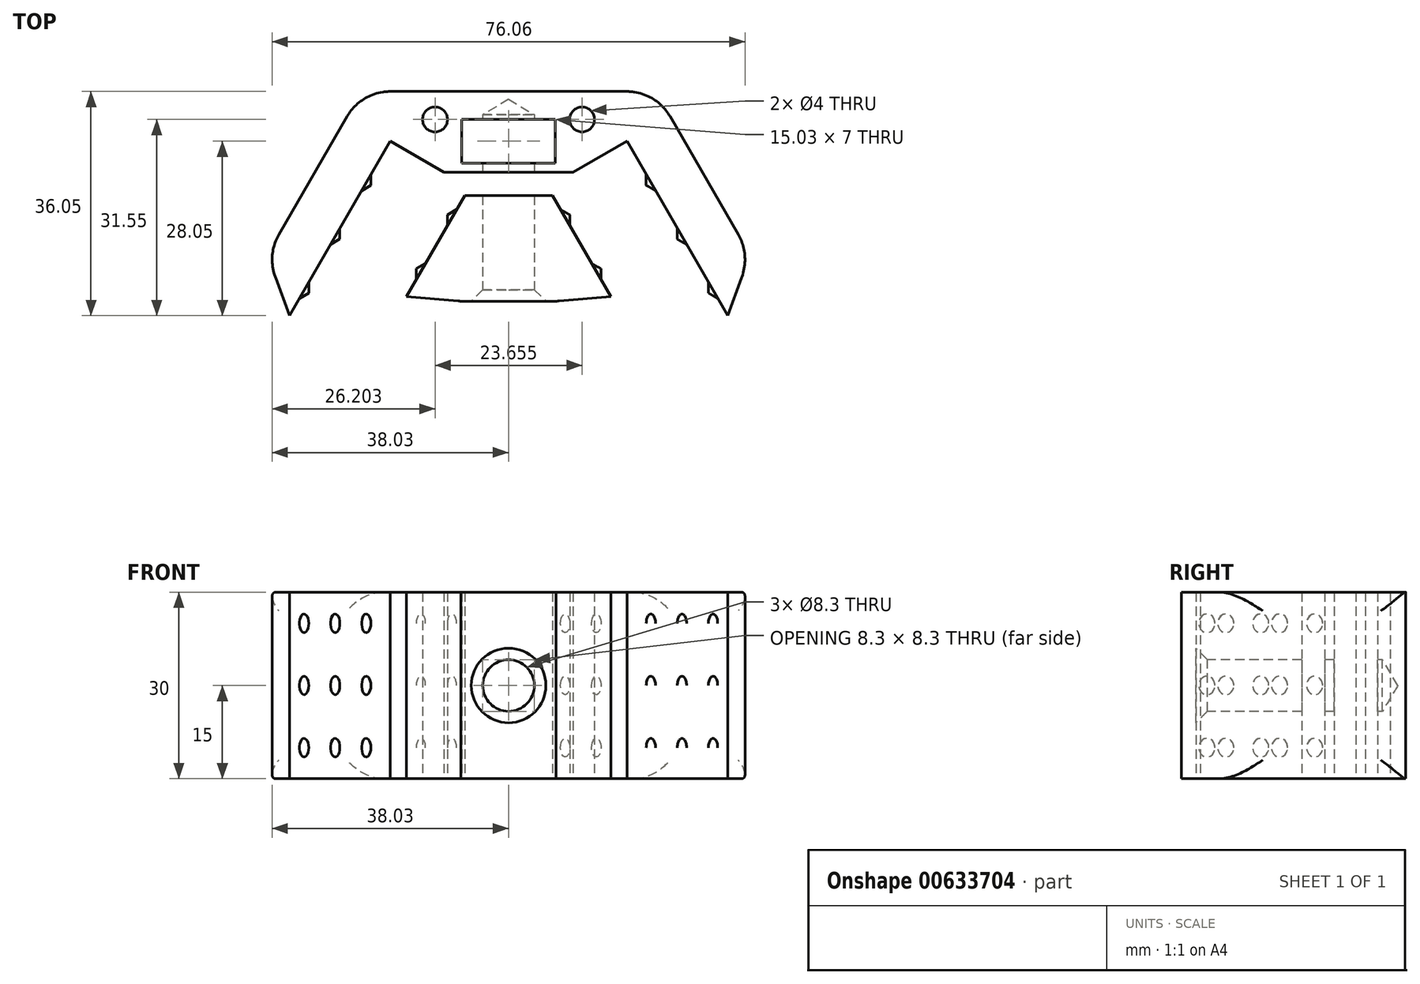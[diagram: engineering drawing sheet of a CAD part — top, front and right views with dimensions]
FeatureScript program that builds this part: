
annotation { "Feature Type Name" : "Feature", "Feature Type Description" : "" }
export const myFeature = defineFeature(function(context is Context, id is Id, definition is map)
    precondition{}
    {
        {
            var Q0;
            Q0=qCreatedBy(makeId("Top.planeOp"),FACE);
            var sketch = newSketch(context, id + "F0", { "sketchPlane" : qUnion([Q0])});
            skLineSegment(sketch, "E0", {"start": v(-3.45, 0) * mm, "end": v(3.45, 0) * mm, "construction": true});
            skLineSegment(sketch, "E1.bottom", {"start": v(3.45, 0) * mm, "end": v(7.06, -6.25) * mm, "construction": true});
            skLineSegment(sketch, "E1.top", {"start": v(19.04, 9) * mm, "end": v(70.61, -80.32) * mm});
            skLineSegment(sketch, "E1.left", {"start": v(3.45, 0) * mm, "end": v(10.38, 4) * mm, "construction": true});
            skLineSegment(sketch, "E2.bottom", {"start": v(-3.45, 0) * mm, "end": v(-7.06, -6.25) * mm, "construction": true});
            skLineSegment(sketch, "E2.top", {"start": v(-19.04, 9) * mm, "end": v(-70.62, -80.34) * mm});
            skLineSegment(sketch, "E2.left", {"start": v(-3.45, 0) * mm, "end": v(-10.38, 4) * mm, "construction": true});
            skLineSegment(sketch, "E3", {"start": v(0, 0) * mm, "end": v(0, 18.24) * mm, "construction": true});
            skLineSegment(sketch, "E4", {"start": v(-19.04, 9) * mm, "end": v(19.04, 9) * mm, "construction": true});
            skLineSegment(sketch, "E5.0", {"start": v(23.66, 17) * mm, "end": v(77.54, -76.32) * mm});
            skLineSegment(sketch, "E5.1", {"start": v(-23.66, 17) * mm, "end": v(23.66, 17) * mm});
            skLineSegment(sketch, "E5.2", {"start": v(-23.66, 17) * mm, "end": v(-77.55, -76.34) * mm});
            skPoint(sketch, "E6", {"position": v(-38.83, -9.27) * mm});
            skLineSegment(sketch, "E7", {"start": v(-38.83, -9.27) * mm, "end": v(-35.24, -19.05) * mm});
            skLineSegment(sketch, "E8.MirrorCS", {"start": v(38.83, -9.27) * mm, "end": v(35.24, -19.05) * mm});
            skLineSegment(sketch, "E9.0", {"start": v(1.16, -8) * mm, "end": v(-48.1, -93.34) * mm});
            skLineSegment(sketch, "E9.1", {"start": v(-1.16, -8) * mm, "end": v(1.16, -8) * mm});
            skLineSegment(sketch, "E9.2", {"start": v(-1.16, -8) * mm, "end": v(48.1, -93.32) * mm});
            skLineSegment(sketch, "E10", {"start": v(-16.45, -22.52) * mm, "end": v(-7.63, -23.24) * mm});
            skLineSegment(sketch, "E11.MirrorCS", {"start": v(16.45, -22.52) * mm, "end": v(7.63, -23.24) * mm});
            skLineSegment(sketch, "E12", {"start": v(-7.64, -23.25) * mm, "end": v(7.64, -23.25) * mm});
            skLineSegment(sketch, "E13", {"start": v(-10.38, 4) * mm, "end": v(10.38, 4) * mm});
            skLineSegment(sketch, "E14", {"start": v(-7.06, -6.25) * mm, "end": v(7.06, -6.25) * mm});
            skLineSegment(sketch, "E15.bottom", {"start": v(7.51, 12.5) * mm, "end": v(-7.51, 12.5) * mm});
            skLineSegment(sketch, "E15.top", {"start": v(7.51, 5.5) * mm, "end": v(-7.51, 5.5) * mm});
            skLineSegment(sketch, "E15.left", {"start": v(7.51, 12.5) * mm, "end": v(7.51, 5.5) * mm});
            skLineSegment(sketch, "E15.right", {"start": v(-7.51, 12.5) * mm, "end": v(-7.51, 5.5) * mm});
            skPoint(sketch, "E15.middle", {"position": v(0, 9) * mm});
            skCircle(sketch, "E16", {"center": v(-11.83, 12.5) * mm, "radius": 2 * mm});
            skCircle(sketch, "E17.MirrorC", {"center": v(11.83, 12.5) * mm, "radius": 2 * mm});
            skLineSegment(sketch, "E18", {"start": v(-10.38, 4) * mm, "end": v(-19.04, 9) * mm});
            skLineSegment(sketch, "E19", {"start": v(-7.06, -6.25) * mm, "end": v(-55.03, -89.34) * mm});
            skLineSegment(sketch, "E20", {"start": v(7.06, -6.25) * mm, "end": v(55.02, -89.32) * mm});
            skLineSegment(sketch, "E21", {"start": v(10.38, 4) * mm, "end": v(19.04, 9) * mm});
            skSolve(sketch);
        }
        {
            var Q0;
            {var subQ9=sQuery(id+"F0.wireOp",EDGE,"E5.1");Q0=makeQuery(id+"F0.imprint","IMPRINT",FACE,{"disambiguationData":[TD([[makeQuery(id+"F0.imprint","IMPRINT",EDGE,{"derivedFrom":subQ9}),-1.0]])]});}
            var Q1;
            {var subQ0=sQuery(id+"F0.wireOp",EDGE,"E10");Q1=makeQuery(id+"F0.imprint","IMPRINT",FACE,{"disambiguationData":[TD([[makeQuery(id+"F0.imprint","IMPRINT",EDGE,{"derivedFrom":subQ0}),1.0]])]});}
            var Q2;
            {var subQ0=sQuery(id+"F0.wireOp",EDGE,"E9.1");Q2=makeQuery(id+"F0.imprint","IMPRINT",FACE,{"disambiguationData":[TD([[makeQuery(id+"F0.imprint","IMPRINT",EDGE,{"derivedFrom":subQ0}),-1.0]])]});}
            var Q3;
            {var subQ5=sQuery(id+"F0.wireOp",EDGE,"E12");Q3=makeQuery(id+"F0.imprint","IMPRINT",FACE,{"disambiguationData":[TD([[makeQuery(id+"F0.imprint","IMPRINT",EDGE,{"derivedFrom":subQ5}),1.0]])]});}
            extrude(context, id + "F1", {"entities" : qUnion([Q0, Q1, Q2, Q3]), "depth" : 30 * mm, "offsetDistance" : 25 * mm});
        }
        {
            var Q0;
            Q0=makeQuery(id+"F1.opExtrude","SWEPT_FACE",FACE,{"disambiguationData":[OSD([sQuery(id+"F0.wireOp",EDGE,"E12")])]});
            var sketch = newSketch(context, id + "F2", { "sketchPlane" : qUnion([Q0])});
            skPoint(sketch, "E22", {"position": v(0, 15) * mm});
            skPoint(sketch, "E22.positionSnap0", {"position": v(0, 30) * mm});
            skPoint(sketch, "E22.positionSnap1", {"position": v(-7.64, 15) * mm});
            skSolve(sketch);
        }
        {
            var Q0;
            Q0=sQuery(id+"F2.wireOp",VERTEX,"E22");
            var Q1;
            Q1=makeQuery(id+"F1.opExtrude","SWEPT_BODY",BODY,{"disambiguationData":[OSD([sQuery(id+"F0.wireOp",EDGE,"E1.top"),sQuery(id+"F0.wireOp",EDGE,"E2.top"),sQuery(id+"F0.wireOp",EDGE,"E5.0"),sQuery(id+"F0.wireOp",EDGE,"E5.1"),sQuery(id+"F0.wireOp",EDGE,"E5.2"),sQuery(id+"F0.wireOp",EDGE,"E7"),sQuery(id+"F0.wireOp",EDGE,"E8.MirrorCS"),sQuery(id+"F0.wireOp",EDGE,"E13"),sQuery(id+"F0.wireOp",EDGE,"E15.bottom"),sQuery(id+"F0.wireOp",EDGE,"E15.top"),sQuery(id+"F0.wireOp",EDGE,"E15.left"),sQuery(id+"F0.wireOp",EDGE,"E15.right"),sQuery(id+"F0.wireOp",EDGE,"E16"),sQuery(id+"F0.wireOp",EDGE,"E17.MirrorC"),sQuery(id+"F0.wireOp",EDGE,"E18"),sQuery(id+"F0.wireOp",EDGE,"E21")])]});
            var Q2;
            Q2=makeQuery(id+"F1.opExtrude","SWEPT_BODY",BODY,{"disambiguationData":[OSD([sQuery(id+"F0.wireOp",EDGE,"E9.0"),sQuery(id+"F0.wireOp",EDGE,"E9.2"),sQuery(id+"F0.wireOp",EDGE,"E10"),sQuery(id+"F0.wireOp",EDGE,"E11.MirrorCS"),sQuery(id+"F0.wireOp",EDGE,"E12"),sQuery(id+"F0.wireOp",EDGE,"E14"),sQuery(id+"F0.wireOp",EDGE,"E19"),sQuery(id+"F0.wireOp",EDGE,"E20")])]});
            hole(context, id + "F3", {"style" : HoleStyle.C_SINK, "endStyle" : HoleEndStyle.BLIND, "holeDiameter" : 8.3 * mm, "cSinkDiameter" : 12 * mm, "cSinkAngle" : 90 * degree, "majorDiameter" : 5 * mm, "holeDepth" : 36.5 * mm, "isTappedThrough" : true, "tappedDepth" : 12 * mm, "tapClearance" : 3, "startFromSketch" : true, "locations" : qUnion([Q0]), "scope" : qUnion([Q1, Q2])});
        }
        {
            var Q0;
            Q0=makeQuery(id+"F1.opExtrude","SWEPT_EDGE",EDGE,{"disambiguationData":[OSD([sQuery(id+"F0.wireOp",EDGE,"E5.2"),sQuery(id+"F0.wireOp",EDGE,"E7")])]});
            var Q1;
            Q1=makeQuery(id+"F1.opExtrude","SWEPT_EDGE",EDGE,{"disambiguationData":[OSD([sQuery(id+"F0.wireOp",EDGE,"E5.1"),sQuery(id+"F0.wireOp",EDGE,"E5.2")])]});
            var Q2;
            Q2=makeQuery(id+"F1.opExtrude","SWEPT_EDGE",EDGE,{"disambiguationData":[OSD([sQuery(id+"F0.wireOp",EDGE,"E5.0"),sQuery(id+"F0.wireOp",EDGE,"E5.1")])]});
            var Q3;
            Q3=makeQuery(id+"F1.opExtrude","SWEPT_EDGE",EDGE,{"disambiguationData":[OSD([sQuery(id+"F0.wireOp",EDGE,"E5.0"),sQuery(id+"F0.wireOp",EDGE,"E8.MirrorCS")])]});
            fillet(context, id + "F4", {"entities" : qUnion([Q0, Q1, Q2, Q3]), "radius" : 8 * mm, "tangentPropagation" : true, "allowEdgeOverflow" : false});
        }
        {
            var Q0;
            Q0=makeQuery(id+"F1.opExtrude","CAP_EDGE",EDGE,{"disambiguationData":[OSD([sQuery(id+"F0.wireOp",EDGE,"E5.0")])],"isStart":false});
            var Q1;
            Q1=makeQuery(id+"F1.opExtrude","CAP_EDGE",EDGE,{"disambiguationData":[OSD([sQuery(id+"F0.wireOp",EDGE,"E5.2")])],"isStart":false});
            var Q2;
            Q2=makeQuery(id+"F1.opExtrude","CAP_EDGE",EDGE,{"disambiguationData":[OSD([sQuery(id+"F0.wireOp",EDGE,"E5.0")])],"isStart":true});
            var Q3;
            Q3=makeQuery(id+"F1.opExtrude","CAP_EDGE",EDGE,{"disambiguationData":[OSD([sQuery(id+"F0.wireOp",EDGE,"E5.2")])],"isStart":true});
            fillet(context, id + "F5", {"entities" : qUnion([Q0, Q1, Q2, Q3]), "radius" : 3 * mm, "allowEdgeOverflow" : false});
        }
        {
            var Q0;
            Q0=makeQuery(id+"F1.opExtrude","SWEPT_EDGE",EDGE,{"disambiguationData":[OSD([sQuery(id+"F0.wireOp",EDGE,"E9.0"),sQuery(id+"F0.wireOp",EDGE,"E10")])]});
            var Q1;
            Q1=makeQuery(id+"F1.opExtrude","SWEPT_EDGE",EDGE,{"disambiguationData":[OSD([sQuery(id+"F0.wireOp",EDGE,"E9.2"),sQuery(id+"F0.wireOp",EDGE,"E11.MirrorCS")])]});
            fillet(context, id + "F6", {"entities" : qUnion([Q0, Q1]), "radius" : 10 * mm, "tangentPropagation" : true, "allowEdgeOverflow" : false});
        }
        {
            var Q0;
            Q0=makeQuery(id+"F1.opExtrude","SWEPT_FACE",FACE,{"disambiguationData":[OSD([sQuery(id+"F0.wireOp",EDGE,"E2.top")])]});
            var sketch = newSketch(context, id + "F7", { "sketchPlane" : qUnion([Q0])});
            skCircle(sketch, "E23", {"center": v(-29.42, 25) * mm, "radius": 1.5 * mm});
            skCircle(sketch, "E24.0.1.0", {"center": v(-29.42, 15) * mm, "radius": 1.5 * mm});
            skCircle(sketch, "E24.0.2.0", {"center": v(-29.42, 5) * mm, "radius": 1.5 * mm});
            skCircle(sketch, "E24.1.0.0", {"center": v(-19.42, 25) * mm, "radius": 1.5 * mm});
            skCircle(sketch, "E24.1.1.0", {"center": v(-19.42, 15) * mm, "radius": 1.5 * mm});
            skCircle(sketch, "E24.1.2.0", {"center": v(-19.42, 5) * mm, "radius": 1.5 * mm});
            skCircle(sketch, "E24.2.0.0", {"center": v(-9.42, 25) * mm, "radius": 1.5 * mm});
            skCircle(sketch, "E24.2.1.0", {"center": v(-9.42, 15) * mm, "radius": 1.5 * mm});
            skCircle(sketch, "E24.2.2.0", {"center": v(-9.42, 5) * mm, "radius": 1.5 * mm});
            skLineSegment(sketch, "E24.direction1", {"start": v(-29.42, 25) * mm, "end": v(-19.42, 25) * mm, "construction": true});
            skLineSegment(sketch, "E24.direction2", {"start": v(-29.42, 25) * mm, "end": v(-29.42, 15) * mm, "construction": true});
            skLineSegment(sketch, "E25", {"start": v(-29.42, 25) * mm, "end": v(-34.12, 25) * mm, "construction": true});
            skLineSegment(sketch, "E26", {"start": v(-29.42, 25) * mm, "end": v(-29.42, 30) * mm, "construction": true});
            skSolve(sketch);
        }
        {
            var Q0;
            Q0=makeQuery(id+"F1.opExtrude","SWEPT_FACE",FACE,{"disambiguationData":[OSD([sQuery(id+"F0.wireOp",EDGE,"E1.top")])]});
            var sketch = newSketch(context, id + "F8", { "sketchPlane" : qUnion([Q0])});
            skCircle(sketch, "E27", {"center": v(9.42, 25) * mm, "radius": 1.5 * mm});
            skCircle(sketch, "E28.0.1.0", {"center": v(9.42, 15) * mm, "radius": 1.5 * mm});
            skCircle(sketch, "E28.0.2.0", {"center": v(9.42, 5) * mm, "radius": 1.5 * mm});
            skCircle(sketch, "E28.1.0.0", {"center": v(19.42, 25) * mm, "radius": 1.5 * mm});
            skCircle(sketch, "E28.1.1.0", {"center": v(19.42, 15) * mm, "radius": 1.5 * mm});
            skCircle(sketch, "E28.1.2.0", {"center": v(19.42, 5) * mm, "radius": 1.5 * mm});
            skCircle(sketch, "E28.2.0.0", {"center": v(29.42, 25) * mm, "radius": 1.5 * mm});
            skCircle(sketch, "E28.2.1.0", {"center": v(29.42, 15) * mm, "radius": 1.5 * mm});
            skCircle(sketch, "E28.2.2.0", {"center": v(29.42, 5) * mm, "radius": 1.5 * mm});
            skLineSegment(sketch, "E28.direction1", {"start": v(9.42, 25) * mm, "end": v(19.42, 25) * mm, "construction": true});
            skLineSegment(sketch, "E28.direction2", {"start": v(9.42, 25) * mm, "end": v(9.42, 15) * mm, "construction": true});
            skLineSegment(sketch, "E29", {"start": v(29.42, 25) * mm, "end": v(34.12, 25) * mm, "construction": true});
            skLineSegment(sketch, "E30", {"start": v(34.12, 25) * mm, "end": v(29.42, 25) * mm, "construction": true});
            skLineSegment(sketch, "E31", {"start": v(29.42, 25) * mm, "end": v(29.42, 30) * mm, "construction": true});
            skSolve(sketch);
        }
        {
            var Q0;
            Q0=makeQuery(id+"F1.opExtrude","SWEPT_FACE",FACE,{"disambiguationData":[OSD([sQuery(id+"F0.wireOp",EDGE,"E19")])]});
            var sketch = newSketch(context, id + "F9", { "sketchPlane" : qUnion([Q0])});
            skCircle(sketch, "E32", {"center": v(13.03, 25) * mm, "radius": 1.5 * mm});
            skCircle(sketch, "E33.0.1.0", {"center": v(13.03, 15) * mm, "radius": 1.5 * mm});
            skCircle(sketch, "E33.0.2.0", {"center": v(13.03, 5) * mm, "radius": 1.5 * mm});
            skCircle(sketch, "E33.1.0.0", {"center": v(23.03, 25) * mm, "radius": 1.5 * mm});
            skCircle(sketch, "E33.1.1.0", {"center": v(23.03, 15) * mm, "radius": 1.5 * mm});
            skCircle(sketch, "E33.1.2.0", {"center": v(23.03, 5) * mm, "radius": 1.5 * mm});
            skLineSegment(sketch, "E33.direction1", {"start": v(13.03, 25) * mm, "end": v(23.03, 25) * mm, "construction": true});
            skLineSegment(sketch, "E33.direction2", {"start": v(13.03, 25) * mm, "end": v(13.03, 15) * mm, "construction": true});
            skLineSegment(sketch, "E34", {"start": v(23.03, 25) * mm, "end": v(23.03, 30) * mm, "construction": true});
            skLineSegment(sketch, "E35", {"start": v(23.03, 25) * mm, "end": v(27.73, 25) * mm, "construction": true});
            skSolve(sketch);
        }
        {
            var Q0;
            Q0=makeQuery(id+"F1.opExtrude","SWEPT_FACE",FACE,{"disambiguationData":[OSD([sQuery(id+"F0.wireOp",EDGE,"E20")])]});
            var sketch = newSketch(context, id + "F10", { "sketchPlane" : qUnion([Q0])});
            skCircle(sketch, "E36", {"center": v(-23.03, 25) * mm, "radius": 1.5 * mm});
            skCircle(sketch, "E37.0.1.0", {"center": v(-23.03, 15) * mm, "radius": 1.5 * mm});
            skCircle(sketch, "E37.0.2.0", {"center": v(-23.03, 5) * mm, "radius": 1.5 * mm});
            skCircle(sketch, "E37.1.0.0", {"center": v(-13.03, 25) * mm, "radius": 1.5 * mm});
            skCircle(sketch, "E37.1.1.0", {"center": v(-13.03, 15) * mm, "radius": 1.5 * mm});
            skCircle(sketch, "E37.1.2.0", {"center": v(-13.03, 5) * mm, "radius": 1.5 * mm});
            skLineSegment(sketch, "E37.direction1", {"start": v(-23.03, 25) * mm, "end": v(-13.03, 25) * mm, "construction": true});
            skLineSegment(sketch, "E37.direction2", {"start": v(-23.03, 25) * mm, "end": v(-23.03, 15) * mm, "construction": true});
            skLineSegment(sketch, "E38", {"start": v(-23.03, 25) * mm, "end": v(-27.73, 25) * mm});
            skLineSegment(sketch, "E39", {"start": v(-27.73, 25) * mm, "end": v(-23.03, 25) * mm, "construction": true});
            skLineSegment(sketch, "E40", {"start": v(-23.03, 25) * mm, "end": v(-23.03, 30) * mm, "construction": true});
            skSolve(sketch);
        }
        {
            var Q0;
            Q0=qSketchRegion(id+"F9",true);
            extrude(context, id + "F11", {"entities" : qUnion([Q0]), "operationType" : NewBodyOperationType.ADD, "depth" : 1 * mm, "offsetDistance" : 25 * mm, "hasDraft" : true, "draftAngle" : 60 * degree, "draftPullDirection" : true});
        }
        {
            var Q0;
            Q0=qSketchRegion(id+"F7",true);
            extrude(context, id + "F12", {"entities" : qUnion([Q0]), "operationType" : NewBodyOperationType.ADD, "depth" : 1 * mm, "offsetDistance" : 25 * mm, "hasDraft" : true, "draftAngle" : 60 * degree, "draftPullDirection" : true});
        }
        {
            var Q0;
            Q0=qSketchRegion(id+"F8",true);
            extrude(context, id + "F13", {"entities" : qUnion([Q0]), "operationType" : NewBodyOperationType.ADD, "depth" : 1 * mm, "offsetDistance" : 25 * mm, "hasDraft" : true, "draftAngle" : 60 * degree, "draftPullDirection" : true});
        }
        {
            var Q0;
            Q0=qSketchRegion(id+"F10",true);
            extrude(context, id + "F14", {"entities" : qUnion([Q0]), "operationType" : NewBodyOperationType.ADD, "depth" : 1 * mm, "offsetDistance" : 25 * mm, "hasDraft" : true, "draftAngle" : 60 * degree, "draftPullDirection" : true});
        }
        {
            var Q0;
            Q0=makeQuery(id+"F1.opExtrude","SWEPT_BODY",BODY,{"disambiguationData":[OSD([sQuery(id+"F0.wireOp",EDGE,"E9.0"),sQuery(id+"F0.wireOp",EDGE,"E9.2"),sQuery(id+"F0.wireOp",EDGE,"E10"),sQuery(id+"F0.wireOp",EDGE,"E11.MirrorCS"),sQuery(id+"F0.wireOp",EDGE,"E12"),sQuery(id+"F0.wireOp",EDGE,"E14"),sQuery(id+"F0.wireOp",EDGE,"E19"),sQuery(id+"F0.wireOp",EDGE,"E20")])]});
            transform(context, id + "F15", {"entities" : qUnion([Q0]), "transformType" : TransformType.TRANSLATION_3D, "dx" : 0 * mm, "dy" : 6.5 * mm, "dz" : 0 * mm, "makeCopy" : false});
        }
    });
